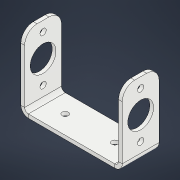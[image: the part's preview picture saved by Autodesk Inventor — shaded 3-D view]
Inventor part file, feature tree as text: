
AUTODESK INVENTOR PART (.ipt)
format: ipt  version: 2022 (Build 260153000, 153)  size: 190,464 bytes
history: native  units: in
note: dims shown in document units (in); Inventor stores cm internally (conversion verified against a paired STEP export)
features: sheet_metal_op x4, sketch x4, hole x3, other x2, projected_geometry x2, fillet x1
ambient origin geometry x8: Origin, YZ Plane, XZ Plane, XY Plane, X Axis, Y Axis, Z Axis, Center Point
bodies: Body1 (feature_tree)
feature tree (16):
  sheet_metal_op  "Face1"
  sheet_metal_op  "Flange1"
  sketch  "Sketch5"  dims[d14=0.16in d15=0.08in]
  hole  "Hole1"  [1 undecoded]
  hole  "Hole2"  [1 undecoded]
  fillet  "Fillet1"  Radius=0.04in
  hole  "Hole3"  [1 undecoded]
  sketch  "Sketch3"  dims[d9=2.1654in d10=0.7874in]
  other  "Plate1"
  sketch  "Sketch4"  dims[d11=0.08in d12=0.08in d13=0.04in]
  other  "Plate2"
  sheet_metal_op  "Bend1"
  sheet_metal_op  "Corner1"
  projected_geometry  "Projected Loop3"
  sketch  "Sketch6"  dims[d16=1.5748in d17=90.0deg d18=0.08in d19=0.32in d20=0.08in d21=0.08in d22=0.4921in d23=0.4921in d24=0.1339in d25=0.2362in d26=0.2559in d27=0.1181in d28=0.6181in d29=0.08in d30=0.8108in d31=0.5512in d32=0.2362in d33=0.1575in d34=0.0787in d35=90.0deg d36=0.315in d37=0.8108in d38=0.2662in d39=0.3937in d40=0.1339in d41=0.2362in d42=0.2559in d43=0.1181in d44=90.0deg d45=0.315in d46=0.8108in d7=0.0197in d8=1.9685in]
  projected_geometry  "Projected Loop4"
note: 3 required parameter values undecoded (feature->parameter linkage not recoverable at this tier; creation-order binding heuristic only, values carry confidence <= 0.55)
